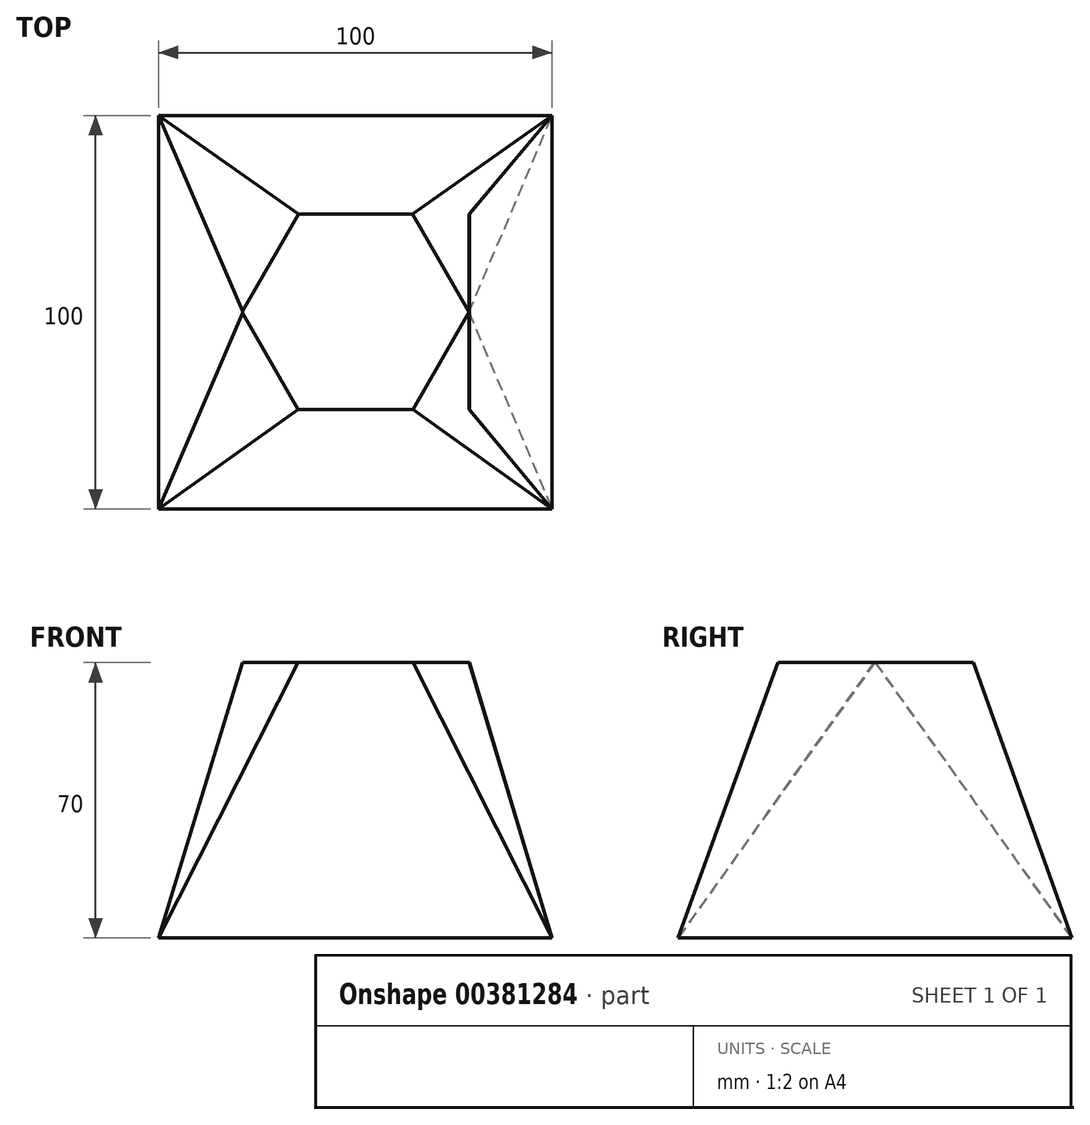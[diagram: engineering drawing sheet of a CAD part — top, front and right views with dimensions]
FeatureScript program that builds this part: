
annotation { "Feature Type Name" : "Feature", "Feature Type Description" : "" }
export const myFeature = defineFeature(function(context is Context, id is Id, definition is map)
    precondition{}
    {
        {
            var Q0;
            Q0=qCreatedBy(makeId("Top.planeOp"),FACE);
            var sketch = newSketch(context, id + "F0", { "sketchPlane" : qUnion([Q0])});
            skLineSegment(sketch, "E0.bottom", {"start": v(50, -50) * mm, "end": v(-50, -50) * mm});
            skLineSegment(sketch, "E0.top", {"start": v(50, 50) * mm, "end": v(-50, 50) * mm});
            skLineSegment(sketch, "E0.left", {"start": v(50, -50) * mm, "end": v(50, 50) * mm});
            skLineSegment(sketch, "E0.right", {"start": v(-50, -50) * mm, "end": v(-50, 50) * mm});
            skPoint(sketch, "E0.middle", {"position": v(0, 0) * mm});
            skSolve(sketch);
        }
        {
            var Q0;
            Q0=makeQuery(id+"F0.imprint","IMPRINT",FACE,{"disambiguationData":[TD([[makeQuery(id+"F0.imprint","IMPRINT",EDGE,{"derivedFrom":sQuery(id+"F0.wireOp",EDGE,"E0.bottom")}),-1.0]])]});
            cPlane(context, id + "F1", {"entities" : qUnion([Q0]), "cplaneType" : CPlaneType.OFFSET, "offset" : 70 * mm, "width" : 150 * mm, "height" : 150 * mm});
        }
        {
            var Q0;
            Q0=qCreatedBy(id+"F1.planeOp",FACE);
            var sketch = newSketch(context, id + "F2", { "sketchPlane" : qUnion([Q0])});
            skCircle(sketch, "E1.cCircle", {"center": v(0, 0) * mm, "radius": 25 * mm, "construction": true});
            skLineSegment(sketch, "E1.0", {"start": v(-14.43, 25) * mm, "end": v(14.43, 25) * mm});
            skLineSegment(sketch, "E1.1", {"start": v(14.43, 25) * mm, "end": v(28.87, 0) * mm});
            skLineSegment(sketch, "E1.2", {"start": v(28.87, 0) * mm, "end": v(14.43, -25) * mm});
            skLineSegment(sketch, "E1.3", {"start": v(14.43, -25) * mm, "end": v(-14.43, -25) * mm});
            skLineSegment(sketch, "E1.4", {"start": v(-14.43, -25) * mm, "end": v(-28.87, 0) * mm});
            skLineSegment(sketch, "E1.5", {"start": v(-28.87, 0) * mm, "end": v(-14.43, 25) * mm});
            skPoint(sketch, "E1.0.midPoint", {"position": v(0, 25) * mm});
            skLineSegment(sketch, "E2.bottom", {"start": v(28.87, 25) * mm, "end": v(-28.87, 25) * mm});
            skLineSegment(sketch, "E2.top", {"start": v(28.87, -25) * mm, "end": v(-28.87, -25) * mm});
            skLineSegment(sketch, "E2.left", {"start": v(28.87, 25) * mm, "end": v(28.87, -25) * mm});
            skLineSegment(sketch, "E2.right", {"start": v(-28.87, 25) * mm, "end": v(-28.87, -25) * mm});
            skSolve(sketch);
        }
        {
            var Q0;
            Q0=qCreatedBy(id+"F1.planeOp",FACE);
            var sketch = newSketch(context, id + "F3", { "sketchPlane" : qUnion([Q0])});
            skLineSegment(sketch, "E3.bottom", {"start": v(-28.72, -24.7) * mm, "end": v(28.98, -24.7) * mm});
            skLineSegment(sketch, "E3.top", {"start": v(-28.72, 24.97) * mm, "end": v(28.98, 24.97) * mm});
            skLineSegment(sketch, "E3.left", {"start": v(-28.72, -24.7) * mm, "end": v(-28.72, 24.97) * mm});
            skLineSegment(sketch, "E3.right", {"start": v(28.98, -24.7) * mm, "end": v(28.98, 24.97) * mm});
            skSolve(sketch);
        }
        {
            var Q0;
            Q0=makeQuery(id+"F0.imprint","IMPRINT",FACE,{"disambiguationData":[TD([[makeQuery(id+"F0.imprint","IMPRINT",EDGE,{"derivedFrom":sQuery(id+"F0.wireOp",EDGE,"E0.bottom")}),-1.0]])]});
            var Q1;
            Q1=makeQuery(id+"F3.imprint","IMPRINT",FACE,{"disambiguationData":[TD([[makeQuery(id+"F3.imprint","IMPRINT",EDGE,{"derivedFrom":sQuery(id+"F3.wireOp",EDGE,"E3.bottom")}),1.0]])]});
            loft(context, id + "F4", {"sheetProfilesArray" : [{ "sheetProfileEntities" : qUnion([Q0]) }, { "sheetProfileEntities" : qUnion([Q1]) }]});
        }
        {
            var Q1;
            {var subQ0=sQuery(id+"F2.wireOp",EDGE,"E1.1");Q1=makeQuery(id+"F2.imprint","IMPRINT",FACE,{"disambiguationData":[TD([[makeQuery(id+"F2.imprint","IMPRINT",EDGE,{"derivedFrom":subQ0}),1.0]])]});}
            var Q2;
            Q2=makeQuery(id+"F4.opLoft","MID_CAP_VERTEX",VERTEX,{"disambiguationData":[OSD([sQuery(id+"F0.wireOp",EDGE,"E0.top"),sQuery(id+"F0.wireOp",EDGE,"E0.left")])],"capPos":0.0});
            loft(context, id + "F5", {"sheetProfilesArray" : [{ "sheetProfileEntities" : qUnion([Q1]) }, { "sheetProfileEntities" : qUnion([Q2]) }]});
        }
        {
            var Q1;
            {var subQ0=sQuery(id+"F2.wireOp",EDGE,"E1.2");Q1=makeQuery(id+"F2.imprint","IMPRINT",FACE,{"disambiguationData":[TD([[makeQuery(id+"F2.imprint","IMPRINT",EDGE,{"derivedFrom":subQ0}),1.0]])]});}
            var Q2;
            Q2=makeQuery(id+"F4.opLoft","MID_CAP_VERTEX",VERTEX,{"disambiguationData":[OSD([sQuery(id+"F0.wireOp",EDGE,"E0.bottom"),sQuery(id+"F0.wireOp",EDGE,"E0.left")])],"capPos":0.0});
            loft(context, id + "F6", {"sheetProfilesArray" : [{ "sheetProfileEntities" : qUnion([Q1]) }, { "sheetProfileEntities" : qUnion([Q2]) }]});
        }
        {
            var Q1;
            {var subQ0=sQuery(id+"F2.wireOp",EDGE,"E1.4");Q1=makeQuery(id+"F2.imprint","IMPRINT",FACE,{"disambiguationData":[TD([[makeQuery(id+"F2.imprint","IMPRINT",EDGE,{"derivedFrom":subQ0}),1.0]])]});}
            var Q2;
            Q2=makeQuery(id+"F4.opLoft","MID_CAP_VERTEX",VERTEX,{"disambiguationData":[OSD([sQuery(id+"F0.wireOp",EDGE,"E0.bottom"),sQuery(id+"F0.wireOp",EDGE,"E0.right")])],"capPos":0.0});
            loft(context, id + "F7", {"sheetProfilesArray" : [{ "sheetProfileEntities" : qUnion([Q1]) }, { "sheetProfileEntities" : qUnion([Q2]) }]});
        }
        {
            var Q1;
            {var subQ0=sQuery(id+"F2.wireOp",EDGE,"E1.5");Q1=makeQuery(id+"F2.imprint","IMPRINT",FACE,{"disambiguationData":[TD([[makeQuery(id+"F2.imprint","IMPRINT",EDGE,{"derivedFrom":subQ0}),1.0]])]});}
            var Q2;
            Q2=makeQuery(id+"F4.opLoft","MID_CAP_VERTEX",VERTEX,{"disambiguationData":[OSD([sQuery(id+"F0.wireOp",EDGE,"E0.top"),sQuery(id+"F0.wireOp",EDGE,"E0.right")])],"capPos":0.0});
            loft(context, id + "F8", {"sheetProfilesArray" : [{ "sheetProfileEntities" : qUnion([Q1]) }, { "sheetProfileEntities" : qUnion([Q2]) }]});
        }
        {
            var Q0;
            {var subQ0=sQuery(id+"F2.wireOp",EDGE,"E1.1");Q0=makeQuery(id+"F5.opLoft","SWEPT_BODY",BODY,{"disambiguationData":[OSD([sQuery(id+"F0.wireOp",EDGE,"E0.top"),sQuery(id+"F0.wireOp",EDGE,"E0.left"),makeQuery(id+"F2.imprint","IMPRINT",FACE,{"disambiguationData":[TD([[makeQuery(id+"F2.imprint","IMPRINT",EDGE,{"derivedFrom":subQ0}),1.0]])]})])]});}
            var Q1;
            {var subQ0=sQuery(id+"F2.wireOp",EDGE,"E1.2");Q1=makeQuery(id+"F6.opLoft","SWEPT_BODY",BODY,{"disambiguationData":[OSD([sQuery(id+"F0.wireOp",EDGE,"E0.bottom"),sQuery(id+"F0.wireOp",EDGE,"E0.left"),makeQuery(id+"F2.imprint","IMPRINT",FACE,{"disambiguationData":[TD([[makeQuery(id+"F2.imprint","IMPRINT",EDGE,{"derivedFrom":subQ0}),1.0]])]})])]});}
            var Q2;
            {var subQ0=sQuery(id+"F2.wireOp",EDGE,"E1.4");Q2=makeQuery(id+"F7.opLoft","SWEPT_BODY",BODY,{"disambiguationData":[OSD([sQuery(id+"F0.wireOp",EDGE,"E0.bottom"),sQuery(id+"F0.wireOp",EDGE,"E0.right"),makeQuery(id+"F2.imprint","IMPRINT",FACE,{"disambiguationData":[TD([[makeQuery(id+"F2.imprint","IMPRINT",EDGE,{"derivedFrom":subQ0}),1.0]])]})])]});}
            var Q3;
            {var subQ0=sQuery(id+"F2.wireOp",EDGE,"E1.5");Q3=makeQuery(id+"F8.opLoft","SWEPT_BODY",BODY,{"disambiguationData":[OSD([sQuery(id+"F0.wireOp",EDGE,"E0.top"),sQuery(id+"F0.wireOp",EDGE,"E0.right"),makeQuery(id+"F2.imprint","IMPRINT",FACE,{"disambiguationData":[TD([[makeQuery(id+"F2.imprint","IMPRINT",EDGE,{"derivedFrom":subQ0}),1.0]])]})])]});}
            var Q4;
            Q4=makeQuery(id+"F4.opLoft","SWEPT_BODY",BODY,{"disambiguationData":[OSD([makeQuery(id+"F0.imprint","IMPRINT",FACE,{"disambiguationData":[TD([[makeQuery(id+"F0.imprint","IMPRINT",EDGE,{"derivedFrom":sQuery(id+"F0.wireOp",EDGE,"E0.bottom")}),-1.0]])]}),makeQuery(id+"F3.imprint","IMPRINT",FACE,{"disambiguationData":[TD([[makeQuery(id+"F3.imprint","IMPRINT",EDGE,{"derivedFrom":sQuery(id+"F3.wireOp",EDGE,"E3.bottom")}),1.0]])]})])]});
            booleanBodies(context, id + "F9", {"operationType" : BooleanOperationType.SUBTRACTION, "tools" : qUnion([Q0, Q1, Q2, Q3]), "targets" : qUnion([Q4])});
        }
    });
